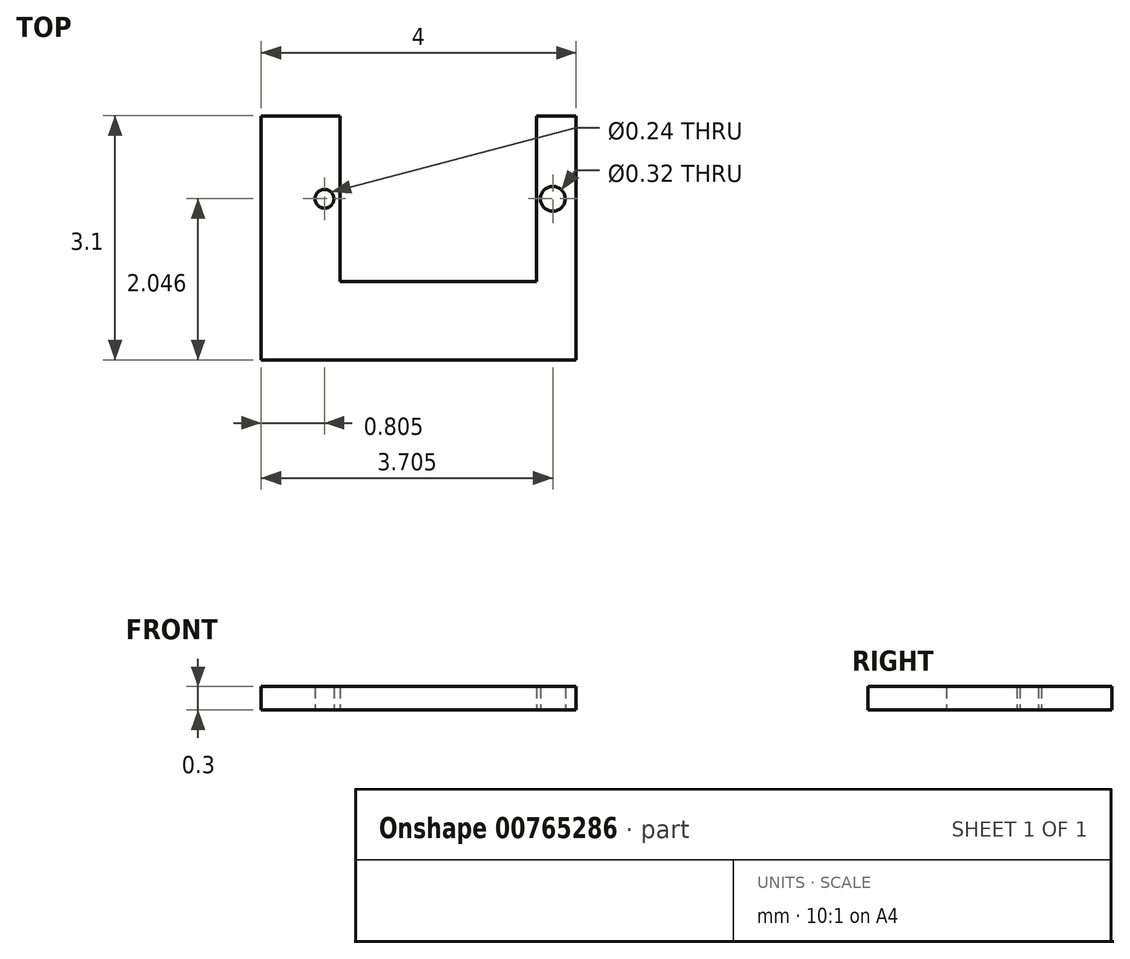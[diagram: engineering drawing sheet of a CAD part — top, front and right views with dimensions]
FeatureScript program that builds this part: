
annotation { "Feature Type Name" : "Feature", "Feature Type Description" : "" }
export const myFeature = defineFeature(function(context is Context, id is Id, definition is map)
    precondition{}
    {
        {
            var Q0;
            Q0=qCreatedBy(makeId("Top.planeOp"),FACE);
            var sketch = newSketch(context, id + "F0", { "sketchPlane" : qUnion([Q0])});
            skLineSegment(sketch, "E0.bottom", {"start": v(-63.06, 27.3) * mm, "end": v(-59.06, 27.3) * mm});
            skLineSegment(sketch, "E0.top", {"start": v(-63.06, 26.3) * mm, "end": v(-59.06, 26.3) * mm});
            skLineSegment(sketch, "E0.left", {"start": v(-63.06, 27.3) * mm, "end": v(-63.06, 26.3) * mm});
            skLineSegment(sketch, "E0.right", {"start": v(-59.06, 27.3) * mm, "end": v(-59.06, 26.3) * mm});
            skLineSegment(sketch, "E1.bottom", {"start": v(-63.06, 27.3) * mm, "end": v(-62.06, 27.3) * mm});
            skLineSegment(sketch, "E1.top", {"start": v(-63.06, 29.4) * mm, "end": v(-62.06, 29.4) * mm});
            skLineSegment(sketch, "E1.left", {"start": v(-63.06, 27.3) * mm, "end": v(-63.06, 29.4) * mm});
            skLineSegment(sketch, "E1.right", {"start": v(-62.06, 27.3) * mm, "end": v(-62.06, 29.4) * mm});
            skLineSegment(sketch, "E2.bottom", {"start": v(-59.06, 27.3) * mm, "end": v(-59.56, 27.3) * mm});
            skLineSegment(sketch, "E3", {"start": v(-59.56, 27.3) * mm, "end": v(-59.56, 29.4) * mm});
            skLineSegment(sketch, "E4", {"start": v(-59.56, 29.4) * mm, "end": v(-59.06, 29.4) * mm});
            skLineSegment(sketch, "E5", {"start": v(-59.06, 29.4) * mm, "end": v(-59.06, 27.3) * mm});
            skCircle(sketch, "E6", {"center": v(-59.36, 28.35) * mm, "radius": 0.16 * mm});
            skPoint(sketch, "E6.centerSnap0", {"position": v(-59.56, 28.35) * mm});
            skCircle(sketch, "E7", {"center": v(-62.26, 28.35) * mm, "radius": 0.12 * mm});
            skPoint(sketch, "E7.centerSnap0", {"position": v(-62.06, 28.35) * mm});
            skSolve(sketch);
        }
        {
            var Q0;
            Q0=makeQuery(id+"F0.imprint","IMPRINT",FACE,{"disambiguationData":[TD([[makeQuery(id+"F0.imprint","IMPRINT",EDGE,{"derivedFrom":sQuery(id+"F0.wireOp",EDGE,"E1.top")}),-1.0]])]});
            var Q1;
            Q1=makeQuery(id+"F0.imprint","IMPRINT",FACE,{"disambiguationData":[TD([[makeQuery(id+"F0.imprint","IMPRINT",EDGE,{"derivedFrom":sQuery(id+"F0.wireOp",EDGE,"E0.top")}),1.0]])]});
            var Q2;
            {var subQ1=sQuery(id+"F0.wireOp",EDGE,"E3");Q2=makeQuery(id+"F0.imprint","IMPRINT",FACE,{"disambiguationData":[TD([[makeQuery(id+"F0.imprint","IMPRINT",EDGE,{"derivedFrom":subQ1}),-1.0]])]});}
            extrude(context, id + "F1", {"entities" : qUnion([Q0, Q1, Q2]), "depth" : 0.3 * mm, "offsetDistance" : 25 * mm});
        }
    });
